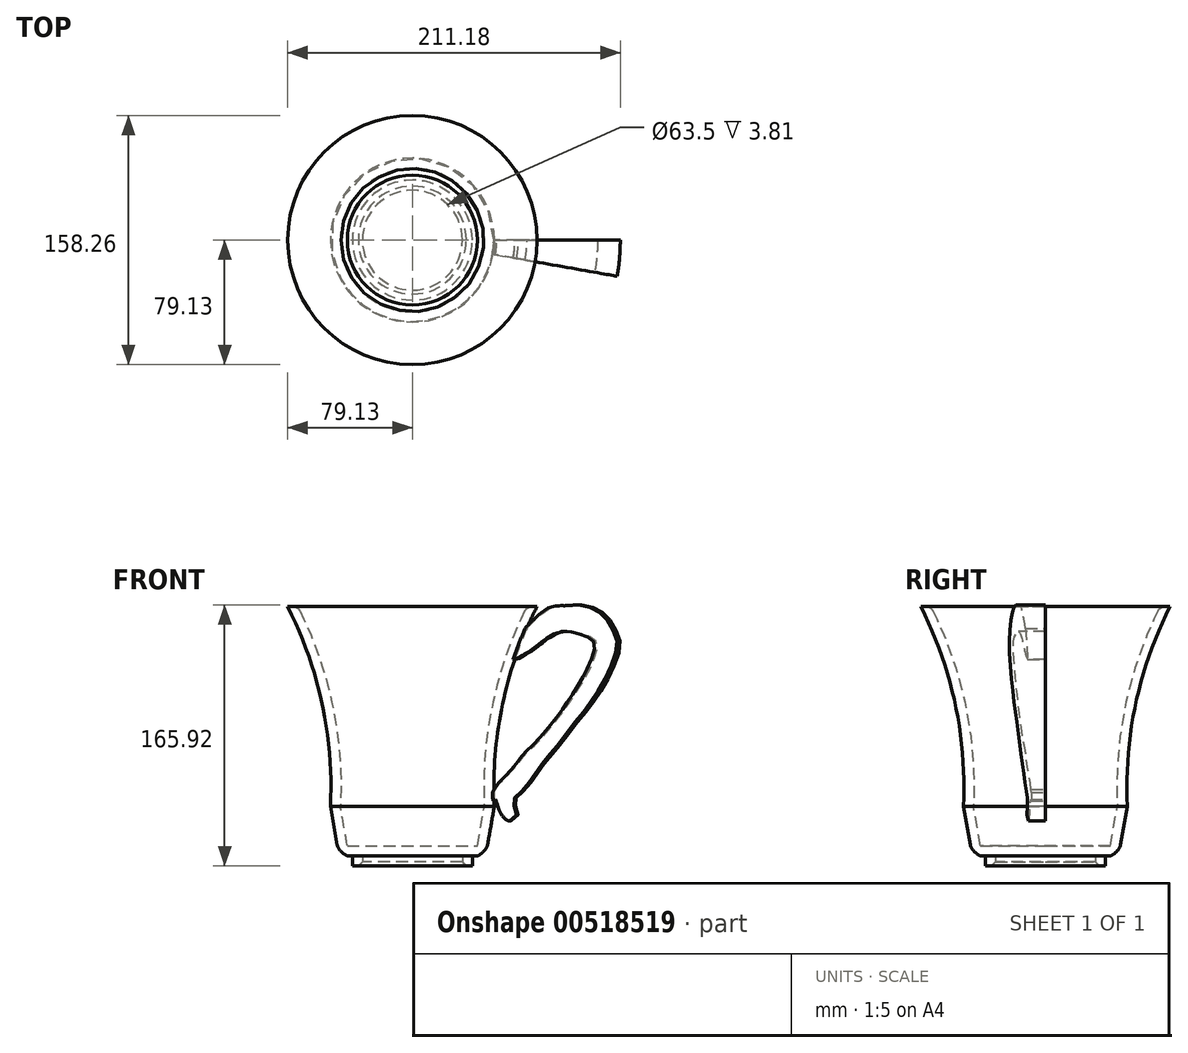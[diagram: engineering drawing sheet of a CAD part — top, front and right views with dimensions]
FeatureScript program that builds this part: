
annotation { "Feature Type Name" : "Feature", "Feature Type Description" : "" }
export const myFeature = defineFeature(function(context is Context, id is Id, definition is map)
    precondition{}
    {
        {
            var Q0;
            Q0=qCreatedBy(makeId("Top.planeOp"),FACE);
            var sketch = newSketch(context, id + "F0", { "sketchPlane" : qUnion([Q0])});
            skCircle(sketch, "E0", {"center": v(0, 0) * mm, "radius": 38.1 * mm});
            skCircle(sketch, "E1", {"center": v(0, 0) * mm, "radius": 31.75 * mm});
            skSolve(sketch);
        }
        {
            var Q0;
            Q0=makeQuery(id+"F0.imprint","IMPRINT",FACE,{"disambiguationData":[TD([[makeQuery(id+"F0.imprint","IMPRINT",EDGE,{"derivedFrom":sQuery(id+"F0.wireOp",EDGE,"E0")}),1.0]])]});
            extrude(context, id + "F1", {"entities" : qUnion([Q0]), "depth" : 6.35 * mm, "offsetDistance" : 25.4 * mm});
        }
        {
            var Q0;
            Q0=makeQuery(id+"F1.opExtrude","CAP_FACE",FACE,{"disambiguationData":[OSD([sQuery(id+"F0.wireOp",EDGE,"E0"),sQuery(id+"F0.wireOp",EDGE,"E1")])],"isStart":false});
            var sketch = newSketch(context, id + "F2", { "sketchPlane" : qUnion([Q0])});
            skCircle(sketch, "E2", {"center": v(0, 0) * mm, "radius": 41.28 * mm});
            skSolve(sketch);
        }
        {
            var Q0;
            Q0=makeQuery(id+"F2.imprint","IMPRINT",FACE,{"disambiguationData":[TD([[makeQuery(id+"F2.imprint","IMPRINT",EDGE,{"derivedFrom":makeQuery(id+"F1.opExtrude","CAP_EDGE",EDGE,{"disambiguationData":[OSD([sQuery(id+"F0.wireOp",EDGE,"E1")])],"isStart":false})}),1.0]])]});
            var Q1;
            Q1=makeQuery(id+"F2.imprint","IMPRINT",FACE,{"disambiguationData":[TD([[makeQuery(id+"F2.imprint","IMPRINT",EDGE,{"derivedFrom":sQuery(id+"F2.wireOp",EDGE,"E2")}),1.0]])]});
            var Q2;
            Q2=makeQuery(id+"F2.imprint","IMPRINT",FACE,{"disambiguationData":[TD([[makeQuery(id+"F2.imprint","IMPRINT",EDGE,{"derivedFrom":makeQuery(id+"F1.opExtrude","CAP_EDGE",EDGE,{"disambiguationData":[OSD([sQuery(id+"F0.wireOp",EDGE,"E0")])],"isStart":false})}),1.0]])]});
            extrude(context, id + "F3", {"entities" : qUnion([Q0, Q1, Q2]), "operationType" : NewBodyOperationType.ADD, "depth" : 6.35 * mm, "offsetDistance" : 25.4 * mm});
        }
        {
            var Q0;
            Q0=qCreatedBy(makeId("Front.planeOp"),FACE);
            var sketch = newSketch(context, id + "F4", { "sketchPlane" : qUnion([Q0])});
            skLineSegment(sketch, "E3", {"start": v(41.28, 12.7) * mm, "end": v(45.69, 37.71) * mm});
            skArc(sketch, "E4", {"start": v(41.28, 6.35) * mm, "mid": v(45, 8.98) * mm, "end": v(47.63, 12.7) * mm});
            skLineSegment(sketch, "E5", {"start": v(47.63, 12.7) * mm, "end": v(52.04, 37.71) * mm});
            skLineSegment(sketch, "E6", {"start": v(45.69, 37.71) * mm, "end": v(52.04, 37.71) * mm});
            skLineSegment(sketch, "E7", {"start": v(41.28, 12.7) * mm, "end": v(41.28, 6.35) * mm});
            skSolve(sketch);
        }
        {
            var Q0;
            Q0=qCreatedBy(makeId("Front.planeOp"),FACE);
            var sketch = newSketch(context, id + "F5", { "sketchPlane" : qUnion([Q0])});
            skLineSegment(sketch, "E8", {"start": v(0, 0) * mm, "end": v(0, 508) * mm});
            skSolve(sketch);
        }
        {
            var Q0;
            Q0=makeQuery(id+"F4.imprint","IMPRINT",FACE,{"disambiguationData":[TD([[makeQuery(id+"F4.imprint","IMPRINT",EDGE,{"derivedFrom":sQuery(id+"F4.wireOp",EDGE,"E3")}),-1.0]])]});
            var Q1;
            Q1=sQuery(id+"F5.wireOp",EDGE,"E8");
            revolve(context, id + "F6", {"operationType" : NewBodyOperationType.ADD, "entities" : qUnion([Q0]), "axis" : qUnion([Q1]), "revolveType" : RevolveType.FULL});
        }
        {
            var Q0;
            Q0=qCreatedBy(makeId("Front.planeOp"),FACE);
            var sketch = newSketch(context, id + "F7", { "sketchPlane" : qUnion([Q0])});
            skArc(sketch, "E9", {"start": v(-52.04, 37.71) * mm, "mid": v(-57.33, 102.97) * mm, "end": v(-79.13, 164.71) * mm});
            skArc(sketch, "E10", {"start": v(-45.69, 37.71) * mm, "mid": v(-50.98, 102.97) * mm, "end": v(-72.78, 164.71) * mm});
            skLineSegment(sketch, "E11", {"start": v(-79.13, 164.71) * mm, "end": v(-72.78, 164.71) * mm});
            skLineSegment(sketch, "E12", {"start": v(-52.04, 37.71) * mm, "end": v(-45.69, 37.71) * mm});
            skSolve(sketch);
        }
        {
            var Q0;
            Q0=makeQuery(id+"F7.imprint","IMPRINT",FACE,{"disambiguationData":[TD([[makeQuery(id+"F7.imprint","IMPRINT",EDGE,{"derivedFrom":sQuery(id+"F7.wireOp",EDGE,"E9")}),-1.0]])]});
            var Q1;
            Q1=makeQuery(id+"F6.opRevolve","SWEPT_FACE",FACE,{"disambiguationData":[OSD([sQuery(id+"F4.wireOp",EDGE,"E3")])]});
            revolve(context, id + "F8", {"operationType" : NewBodyOperationType.ADD, "entities" : qUnion([Q0]), "axis" : qUnion([Q1]), "revolveType" : RevolveType.FULL});
        }
        {
            var Q0;
            Q0=qCreatedBy(makeId("Front.planeOp"),FACE);
            var sketch = newSketch(context, id + "F9", { "sketchPlane" : qUnion([Q0])});
            skFitSpline(sketch, "E13", {"points": [v(72.5, 150.81) * mm, v(78.67, 156.98) * mm, v(89.25, 164.48) * mm, v(99.83, 165.36) * mm, v(109.53, 165.8) * mm, v(117.9, 162.71) * mm, v(124.08, 158.3) * mm, v(128.93, 150.37) * mm, v(132.01, 142) * mm, v(129.8, 131.42) * mm, v(124.08, 118.2) * mm, v(117.02, 107.17) * mm, v(110.85, 98.35) * mm, v(102.92, 89.1) * mm, v(93.66, 76.75) * mm, v(87.93, 70.14) * mm, v(80.44, 60.44) * mm, v(76.47, 54.71) * mm, v(70.3, 47.22) * mm, v(65.89, 43.25) * mm, v(65.45, 38.4) * mm, v(67.21, 33.11) * mm, v(63.24, 28.7) * mm, v(58.4, 31.35) * mm, v(55.75, 36.2) * mm, v(53.55, 42.37) * mm, v(52.66, 48.54) * mm, v(59.28, 56.48) * mm, v(66.33, 63.97) * mm, v(72.5, 71.9) * mm, v(79.55, 78.52) * mm, v(93.66, 95.27) * mm, v(100.27, 104.53) * mm, v(108.2, 116.87) * mm, v(113.94, 127.89) * mm, v(117.46, 141.11) * mm, v(111.73, 145.96) * mm, v(102.48, 148.6) * mm, v(97.63, 149.05) * mm, v(87.93, 145.52) * mm, v(77.8, 138.03) * mm, v(70.74, 133.62) * mm, v(64.57, 131.42) * mm, v(67.65, 143.76) * mm, v(72.5, 150.81) * mm]});
            skLineSegment(sketch, "E14", {"start": v(53.55, 42.37) * mm, "end": v(48.08, 39.15) * mm});
            skLineSegment(sketch, "E15", {"start": v(48.08, 39.15) * mm, "end": v(52.66, 48.54) * mm});
            skSolve(sketch);
        }
        {
            var Q0;
            {var subQ0=sQuery(id+"F9.wireOp",EDGE,"E13");var subQ1=makeQuery(id+"F9.imprint","INTERSECT",VERTEX,{"derivedFrom":[subQ0,sQuery(id+"F9.wireOp",EDGE,"E14")]});Q0=makeQuery(id+"F9.imprint","IMPRINT",FACE,{"disambiguationData":[TD([[makeQuery(id+"F9.imprint","IMPRINT",EDGE,{"disambiguationData":[TD([[subQ1,-1.0]])],"derivedFrom":subQ0}),-1.0]])]});}
            var Q1;
            {var subQ0=sQuery(id+"F9.wireOp",EDGE,"E14");Q1=makeQuery(id+"F9.imprint","IMPRINT",FACE,{"disambiguationData":[TD([[makeQuery(id+"F9.imprint","IMPRINT",EDGE,{"derivedFrom":subQ0}),-1.0]])]});}
            var Q2;
            Q2=makeQuery(id+"F8.opRevolve","SWEPT_FACE",FACE,{"disambiguationData":[OSD([sQuery(id+"F7.wireOp",EDGE,"E9")])]});
            revolve(context, id + "F10", {"operationType" : NewBodyOperationType.ADD, "entities" : qUnion([Q0, Q1]), "axis" : qUnion([Q2]), "revolveType" : RevolveType.ONE_DIRECTION, "angle" : 10 * degree});
        }
        {
            var Q0;
            Q0=makeQuery(id+"F8.opRevolve","SWEPT_EDGE",EDGE,{"disambiguationData":[OSD([sQuery(id+"F7.wireOp",EDGE,"E10"),sQuery(id+"F7.wireOp",EDGE,"E11")])]});
            fillet(context, id + "F11", {"entities" : qUnion([Q0]), "radius" : 5.08 * mm, "tangentPropagation" : true, "allowEdgeOverflow" : false});
        }
        {
            var Q0;
            Q0=makeQuery(id+"F6.opRevolve","SWEPT_EDGE",EDGE,{"disambiguationData":[OSD([sQuery(id+"F4.wireOp",EDGE,"E4"),sQuery(id+"F4.wireOp",EDGE,"E5")])]});
            fillet(context, id + "F12", {"entities" : qUnion([Q0]), "radius" : 5.08 * mm, "tangentPropagation" : true, "allowEdgeOverflow" : false});
        }
        {
            var Q0;
            Q0=makeQuery(id+"F1.opExtrude","CAP_EDGE",EDGE,{"disambiguationData":[OSD([sQuery(id+"F0.wireOp",EDGE,"E1")])],"isStart":true});
            chamfer(context, id + "F13", {"entities" : qUnion([Q0]), "width" : 2.54 * mm, "tangentPropagation" : true});
        }
    });
